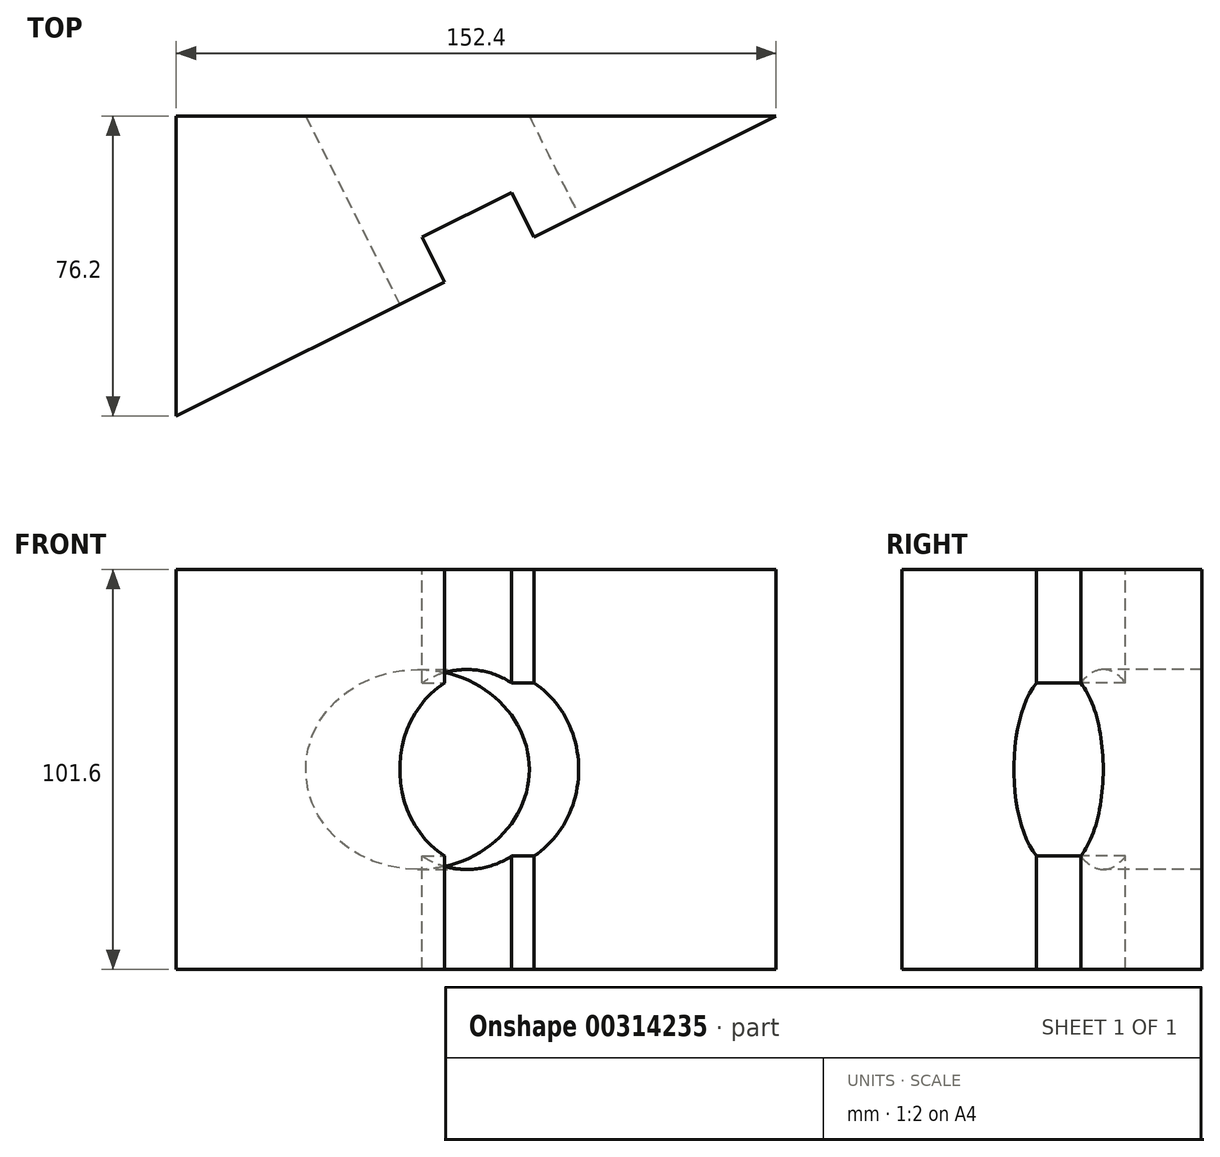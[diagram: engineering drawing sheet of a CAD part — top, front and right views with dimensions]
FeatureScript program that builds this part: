
annotation { "Feature Type Name" : "Feature", "Feature Type Description" : "" }
export const myFeature = defineFeature(function(context is Context, id is Id, definition is map)
    precondition{}
    {
        {
            var Q0;
            Q0=qCreatedBy(makeId("Top.planeOp"),FACE);
            var sketch = newSketch(context, id + "F0", { "sketchPlane" : qUnion([Q0])});
            skLineSegment(sketch, "E0.bottom", {"start": v(-46.35, -2.52) * mm, "end": v(106.05, -2.52) * mm});
            skLineSegment(sketch, "E0.top", {"start": v(-46.35, -78.72) * mm, "end": v(106.05, -78.72) * mm});
            skLineSegment(sketch, "E0.left", {"start": v(-46.35, -2.52) * mm, "end": v(-46.35, -78.72) * mm});
            skLineSegment(sketch, "E0.right", {"start": v(106.05, -2.52) * mm, "end": v(106.05, -78.72) * mm});
            skLineSegment(sketch, "E1", {"start": v(106.05, -2.52) * mm, "end": v(-46.35, -78.72) * mm});
            skSolve(sketch);
        }
        {
            var Q0;
            Q0=makeQuery(id+"F0.imprint","IMPRINT",FACE,{"disambiguationData":[TD([[makeQuery(id+"F0.imprint","IMPRINT",EDGE,{"derivedFrom":sQuery(id+"F0.wireOp",EDGE,"E0.bottom")}),-1.0]])]});
            extrude(context, id + "F1", {"entities" : qUnion([Q0]), "depth" : 101.6 * mm});
        }
        {
            var Q0;
            Q0=makeQuery(id+"F1.opExtrude","SWEPT_FACE",FACE,{"disambiguationData":[OSD([sQuery(id+"F0.wireOp",EDGE,"E1")])]});
            var sketch = newSketch(context, id + "F2", { "sketchPlane" : qUnion([Q0])});
            skLineSegment(sketch, "E2.bottom", {"start": v(24.94, 0) * mm, "end": v(-0.46, 0) * mm});
            skLineSegment(sketch, "E2.top", {"start": v(24.94, 101.6) * mm, "end": v(-0.46, 101.6) * mm});
            skLineSegment(sketch, "E2.left", {"start": v(24.94, 0) * mm, "end": v(24.94, 101.6) * mm});
            skLineSegment(sketch, "E2.right", {"start": v(-0.46, 0) * mm, "end": v(-0.46, 101.6) * mm});
            skPoint(sketch, "E2.middle", {"position": v(12.24, 50.8) * mm});
            skSolve(sketch);
        }
        {
            var Q0;
            {var subQ0=sQuery(id+"F2.wireOp",EDGE,"E2.left");Q0=makeQuery(id+"F2.imprint","IMPRINT",FACE,{"disambiguationData":[TD([[makeQuery(id+"F2.imprint","IMPRINT",EDGE,{"derivedFrom":subQ0}),-1.0]])]});}
            var sketch = newSketch(context, id + "F3", { "sketchPlane" : qUnion([Q0])});
            skCircle(sketch, "E3", {"center": v(12.24, 50.8) * mm, "radius": 25.4 * mm});
            skSolve(sketch);
        }
        {
            var Q0;
            Q0=makeQuery(id+"F2.imprint","IMPRINT",FACE,{"disambiguationData":[TD([[makeQuery(id+"F2.imprint","IMPRINT",EDGE,{"derivedFrom":sQuery(id+"F2.wireOp",EDGE,"E2.bottom")}),-1.0]])]});
            extrude(context, id + "F4", {"entities" : qUnion([Q0]), "operationType" : NewBodyOperationType.REMOVE, "oppositeDirection" : true, "depth" : 12.7 * mm});
        }
        {
            var Q0;
            Q0 = qSketchRegion(id + "F3", true);
            extrude(context, id + "F5", {"entities" : qUnion([Q0]), "operationType" : NewBodyOperationType.REMOVE, "oppositeDirection" : true, "depth" : 110.49 * mm});
        }
    });
